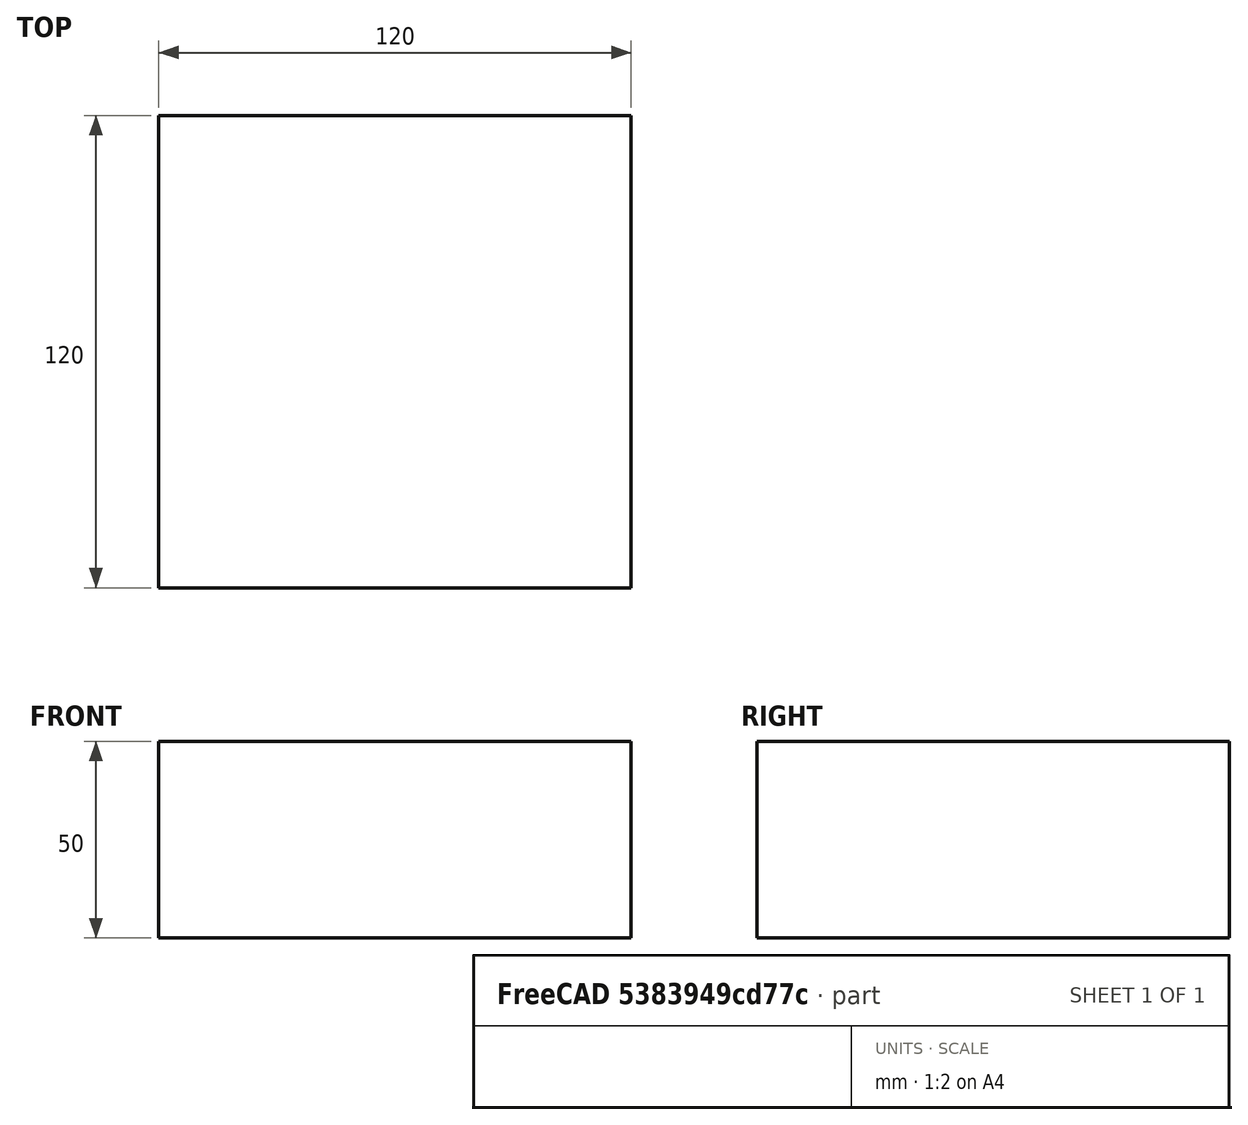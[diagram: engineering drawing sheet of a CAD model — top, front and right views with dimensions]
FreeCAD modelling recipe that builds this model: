
FCSTD DOCUMENT  (FreeCAD 0.15R4671 (Git))
Label: Square Bar 120 EN10059 S235JR
License: All rights reserved
LicenseURL: http://en.wikipedia.org/wiki/All_rights_reserved
objects: Sketcher::SketchObject×1, Part::Extrusion×1
note: 2 computed .brp shape members not serialized (recipe doc carries the construction recipe); baked Part::Feature solids carry a one-line shape summary decoded from their .brp

FEATURE [Sketcher::SketchObject] Sketch
  sketch-geometry (4):
    g0: LineSegment StartX=-60 StartY=-60 StartZ=0 EndX=60 EndY=-60 EndZ=0
    g1: LineSegment StartX=60 StartY=-60 StartZ=0 EndX=60 EndY=60 EndZ=0
    g2: LineSegment StartX=60 StartY=60 StartZ=0 EndX=-60 EndY=60 EndZ=0
    g3: LineSegment StartX=-60 StartY=60 StartZ=0 EndX=-60 EndY=-60 EndZ=0
  constraints (12):
    c: Coincident(g0,g1)
    c: Coincident(g1,g2)
    c: Coincident(g2,g3)
    c: Coincident(g3,g0)
    c: Horizontal(g0)
    c: Horizontal(g2)
    c: Vertical(g1)
    c: Vertical(g3)
    c: Symmetric(g1,g0,g-1)
    c: Symmetric(g2,g1,g-2)
    c: Equal(g1,g2)
    c: DistanceY(g1) = 120
FEATURE [Part::Extrusion] Extrude  label="Square Bar 120 EN10059 S235JR"
  Base = -> Sketch
  Dir = (0,0,50)
  Solid = true
